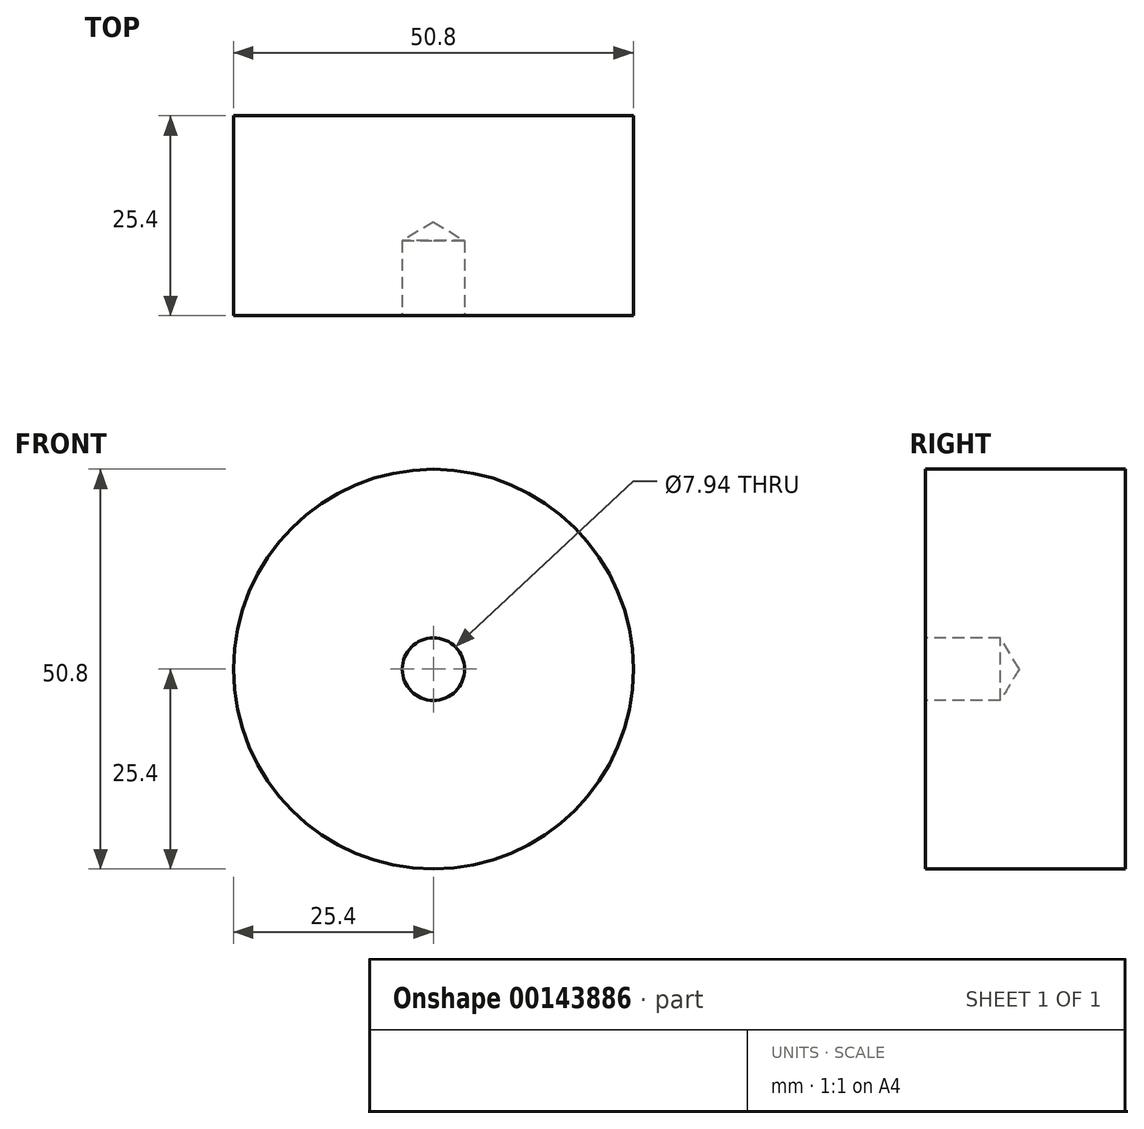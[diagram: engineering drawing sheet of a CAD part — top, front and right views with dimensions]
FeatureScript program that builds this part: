
annotation { "Feature Type Name" : "Feature", "Feature Type Description" : "" }
export const myFeature = defineFeature(function(context is Context, id is Id, definition is map)
    precondition{}
    {
        {
            var Q0;
            Q0=qCreatedBy(makeId("Front.planeOp"),FACE);
            var sketch = newSketch(context, id + "F0", { "sketchPlane" : qUnion([Q0])});
            skCircle(sketch, "E0", {"center": v(0, 0) * mm, "radius": 25.4 * mm});
            skSolve(sketch);
        }
        {
            var Q0;
            Q0=makeQuery(id+"F0.imprint","IMPRINT",FACE,{"disambiguationData":[TD([[makeQuery(id+"F0.imprint","IMPRINT",EDGE,{"derivedFrom":sQuery(id+"F0.wireOp",EDGE,"E0")}),1.0]])]});
            extrude(context, id + "F1", {"entities" : qUnion([Q0]), "depth" : 25.4 * mm});
        }
        {
            var Q0;
            Q0=makeQuery(id+"F1.opExtrude","CAP_FACE",FACE,{"disambiguationData":[OSD([sQuery(id+"F0.wireOp",EDGE,"E0")])],"isStart":false});
            var sketch = newSketch(context, id + "F2", { "sketchPlane" : qUnion([Q0])});
            skPoint(sketch, "E1", {"position": v(0, 0) * mm});
            skSolve(sketch);
        }
        {
            var Q0;
            Q0=sQuery(id+"F2.wireOp",VERTEX,"E1");
            var Q1;
            Q1=makeQuery(id+"F1.opExtrude","SWEPT_BODY",BODY,{"disambiguationData":[OSD([sQuery(id+"F0.wireOp",EDGE,"E0")])]});
            hole(context, id + "F3", {"style" : HoleStyle.SIMPLE, "endStyle" : HoleEndStyle.BLIND, "standardTappedOrClearance" : lookupTablePath({ "standard" : "ANSI", "engagement" : "75%", "pitch" : "16 tpi", "size" : "3/8", "type" : "Tapped" }), "standardBlindInLast" : lookupTablePath({ "standard" : "ANSI", "engagement" : "75%", "pitch" : "16 tpi", "size" : "3/8", "type" : "Tapped" }), "holeDiameter" : 7.94 * mm, "holeDepth" : 9.52 * mm, "locations" : qUnion([Q0]), "scope" : qUnion([Q1]), "majorDiameter" : 9.53 * mm});
        }
    });
